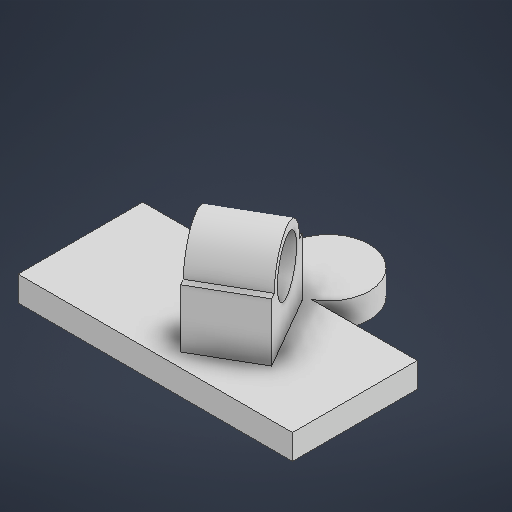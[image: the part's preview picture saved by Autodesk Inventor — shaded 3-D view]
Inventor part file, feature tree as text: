
AUTODESK INVENTOR PART (.ipt)
format: ipt  version: 2025.3 (Build 293356000, 356)  size: 224,768 bytes
history: native  units: in
note: dims shown in document units (in); Inventor stores cm internally (conversion verified against a paired STEP export)
features: other x3, extrude x1, sketch x1
ambient origin geometry x8: Origin, YZ Plane, XZ Plane, XY Plane, X Axis, Y Axis, Z Axis, Center Point
bodies: Solid1 (feature_tree)
feature tree (5):
  other  "Nozzle Fixer.ipt"
  extrude  "Extrusion1"  Depth=0.3937in
  other  "Solid1::Nozzle Fixer.ipt"
  other  "TaggingFeature1"
  sketch  "Sketch1"  dims[d0=0.3937in d1=0.1969in d2=0.0787in d3=0.3937in d4=0.0in]
